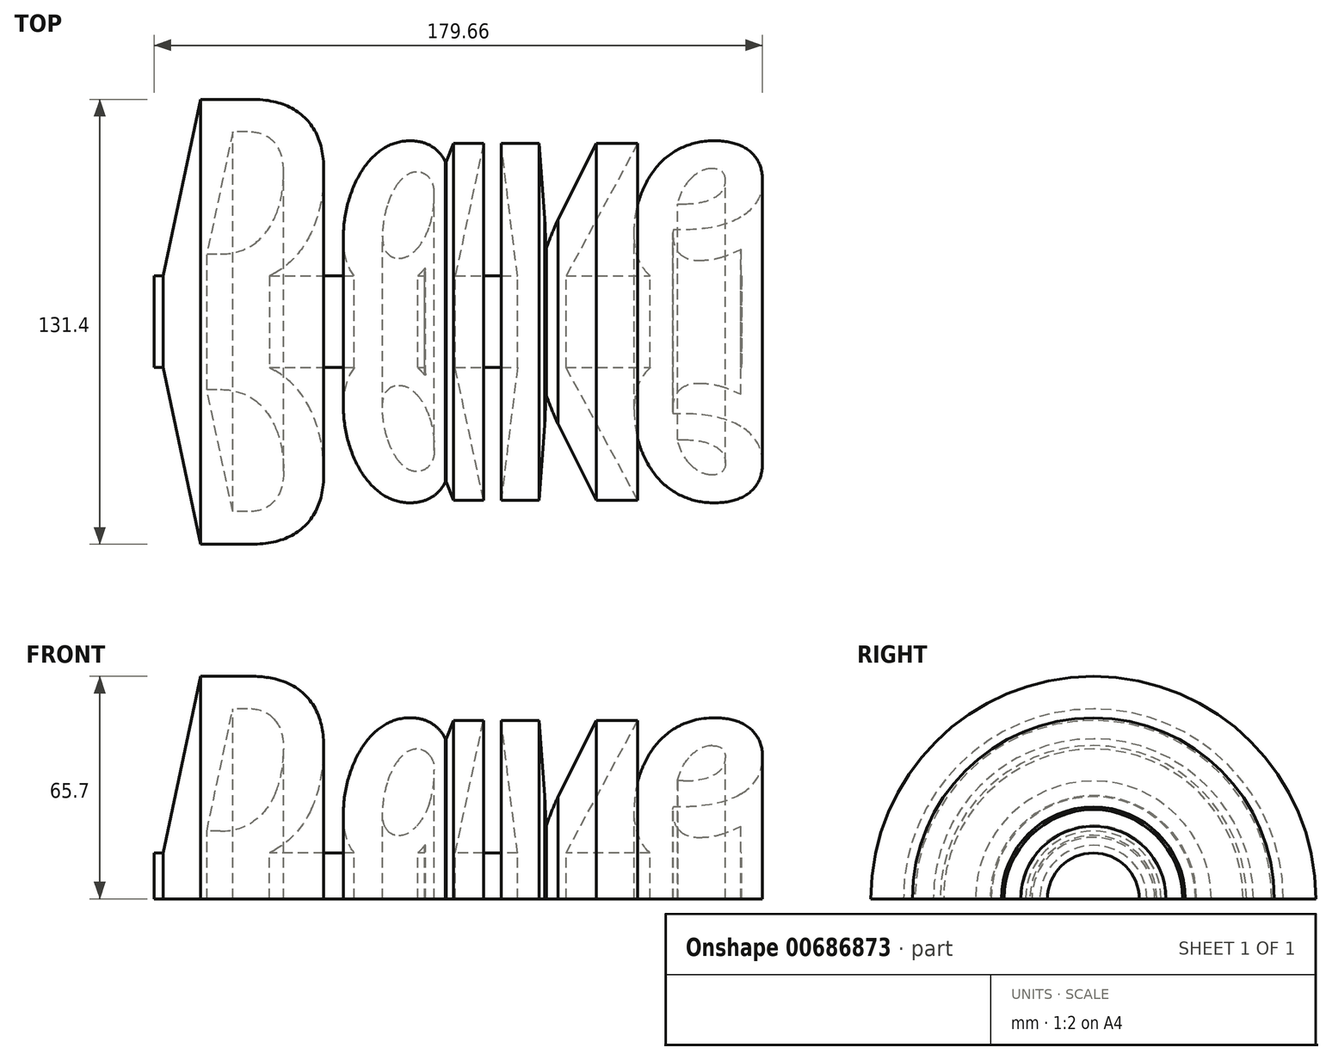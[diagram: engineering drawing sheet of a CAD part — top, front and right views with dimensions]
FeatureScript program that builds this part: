
annotation { "Feature Type Name" : "Feature", "Feature Type Description" : "" }
export const myFeature = defineFeature(function(context is Context, id is Id, definition is map)
    precondition{}
    {
        {
            var Q0;
            Q0=qCreatedBy(makeId("Top.planeOp"),FACE);
            var sketch = newSketch(context, id + "F0", { "sketchPlane" : qUnion([Q0])});
            skText(sketch, "E0", { "text": "Dave", "fontName": "OpenSans-BoldItalic.ttf"});
            skLineSegment(sketch, "E1.bottom", {"start": v(0, -10.3) * mm, "end": v(173.54, -10.3) * mm});
            skLineSegment(sketch, "E1.top", {"start": v(0, 3.23) * mm, "end": v(173.54, 3.23) * mm});
            skLineSegment(sketch, "E1.left", {"start": v(0, -10.3) * mm, "end": v(0, 3.23) * mm});
            skLineSegment(sketch, "E1.right", {"start": v(173.54, -10.3) * mm, "end": v(173.54, 3.23) * mm});
            const initialGuessF0  = {"E0": [0, 0, 1, 0, 0.05587]};
            skSetInitialGuess(sketch, initialGuessF0);
            skSolve(sketch);
        }
        {
            var Q0;
            Q0 = qSketchRegion(id + "F0", true);
            var Q1;
            Q1=sQuery(id+"F0.wireOp",EDGE,"E1.bottom");
            revolve(context, id + "F1", {"entities" : qUnion([Q0]), "axis" : qUnion([Q1]), "revolveType" : RevolveType.ONE_DIRECTION, "angle" : 180 * degree});
        }
    });
